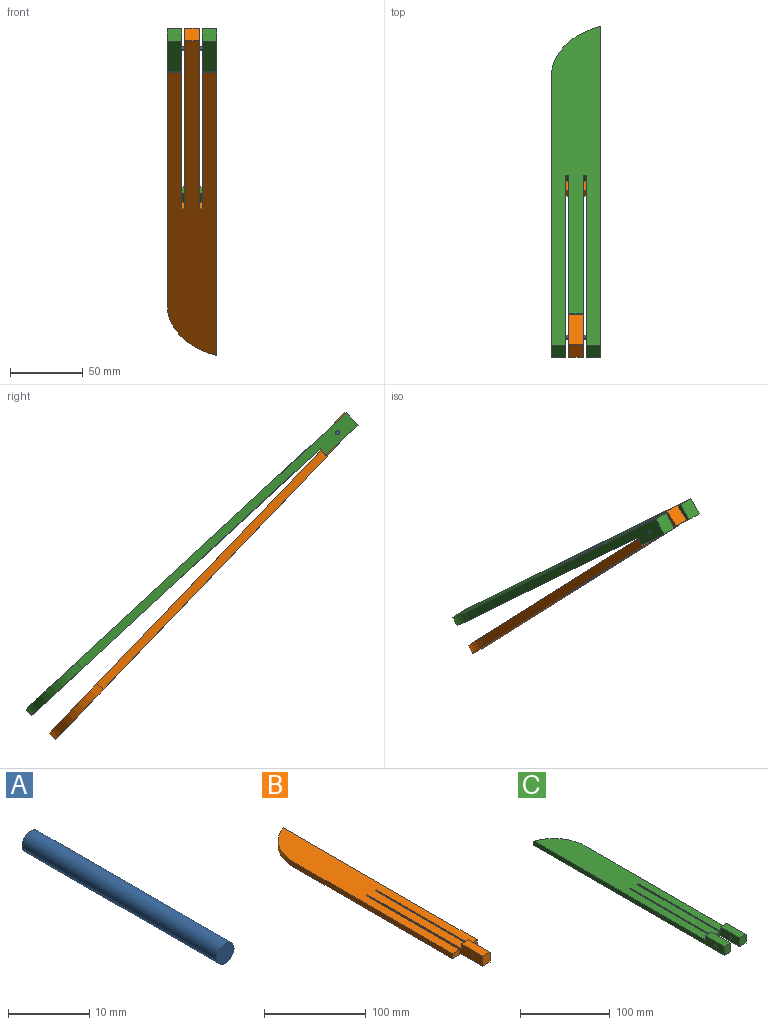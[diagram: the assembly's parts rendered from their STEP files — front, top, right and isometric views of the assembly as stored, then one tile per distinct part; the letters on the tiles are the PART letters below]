
ASSEMBLY  parts=3 mates=3
PART A: 3 faces, bbox 3x34x3 mm
  f0: cylinder r=1.5mm len=34mm, axis (0,1,0), area 320.4mm2, adj f1,f2
  f1: plane 3x3mm, normal (0,-1,0), area 7.1mm2, adj f0
  f2: plane 3x3mm, normal (0,1,0), area 7.1mm2, adj f0
PART B: 17 faces, bbox 34x300x12 mm
  f0: plane 270x34mm, normal (0,0,1), area 8226.8mm2, adj f1,f3,f4,f5,f6,f7,f8,f9
  f1: plane 160x12mm, normal (-1,0,0), area 1132.9mm2, adj f0,f2,f11,f12,f14,f15,f16
  f2: plane 12x10mm, normal (0,-1,0), area 120mm2, adj f1,f3,f12,f15
  f3: plane 160x12mm, normal (1,0,0), area 1132.9mm2, adj f0,f2,f4,f12,f14,f15,f16
  f4: plane 6x2mm, normal (0,-1,0), area 12mm2, adj f0,f3,f5,f12
  f5: plane 130x6mm, normal (-1,0,0), area 780mm2, adj f0,f4,f6,f12
  f6: plane 10x6mm, normal (0,-1,0), area 60mm2, adj f0,f5,f7,f12
  f7: plane 270x6mm, normal (1,0,0), area 1620mm2, adj f0,f6,f12,f13
  f8: plane 222.63x6mm, normal (-1,0,0), area 1335.8mm2, adj f0,f9,f12,f13
  f9: plane 10x6mm, normal (0,-1,0), area 60mm2, adj f0,f8,f10,f12
  f10: plane 130x6mm, normal (1,0,0), area 780mm2, adj f0,f9,f11,f12
  f11: plane 6x2mm, normal (0,-1,0), area 12mm2, adj f0,f1,f10,f12
  f12: plane 300x34mm, normal (0,0,-1), area 8526.8mm2, adj f1,f2,f3,f4,f5,f6,f7,f8
  f13: cylinder r=50mm len=47.37mm, axis (0,0,-1), area 373.5mm2, adj f0,f7,f8,f12
  f14: plane 10x6mm, normal (0,1,0), area 60mm2, adj f0,f1,f3,f15
  f15: plane 30x10mm, normal (0,0,1), area 300mm2, adj f1,f2,f3,f14
  f16: cylinder r=1.5mm len=10mm, axis (-1,0,0), area 94.2mm2, adj f1,f3
PART C: 20 faces, bbox 34x300x12 mm
  f0: plane 270x34mm, normal (0,0,1), area 8226.8mm2, adj f1,f2,f3,f4,f5,f6,f7,f9
  f1: plane 160x12mm, normal (1,0,0), area 1132.9mm2, adj f0,f2,f11,f12,f13,f14,f18
  f2: plane 6x2mm, normal (0,-1,0), area 12mm2, adj f0,f1,f3,f12
  f3: plane 130x6mm, normal (-1,0,0), area 780mm2, adj f0,f2,f4,f12
  f4: plane 10x6mm, normal (0,-1,0), area 60mm2, adj f0,f3,f5,f12
  f5: plane 130x6mm, normal (1,0,0), area 780mm2, adj f0,f4,f6,f12
  f6: plane 6x2mm, normal (0,-1,0), area 12mm2, adj f0,f5,f7,f12
  f7: plane 160x12mm, normal (-1,0,0), area 1132.9mm2, adj f0,f6,f8,f12,f15,f16,f17
  f8: plane 12x10mm, normal (0,-1,0), area 120mm2, adj f7,f9,f12,f16
  f9: plane 252.63x12mm, normal (1,0,0), area 1688.7mm2, adj f0,f8,f12,f15,f16,f17,f19
  f10: plane 300x12mm, normal (-1,0,0), area 1972.9mm2, adj f0,f11,f12,f13,f14,f18,f19
  f11: plane 12x10mm, normal (0,-1,0), area 120mm2, adj f1,f10,f12,f14
  f12: plane 300x34mm, normal (0,0,-1), area 8826.8mm2, adj f1,f2,f3,f4,f5,f6,f7,f8
  f13: plane 10x6mm, normal (0,1,0), area 60mm2, adj f0,f1,f10,f14
  f14: plane 30x10mm, normal (0,0,1), area 300mm2, adj f1,f10,f11,f13
  f15: plane 10x6mm, normal (0,1,0), area 60mm2, adj f0,f7,f9,f16
  f16: plane 30x10mm, normal (0,0,1), area 300mm2, adj f7,f8,f9,f15
  f17: cylinder r=1.5mm len=10mm, axis (-1,0,0), area 94.2mm2, adj f7,f9
  f18: cylinder r=1.5mm len=10mm, axis (-1,0,0), area 94.2mm2, adj f1,f10
  f19: cylinder r=50mm len=47.37mm, axis (0,0,-1), area 373.5mm2, adj f0,f9,f10,f12
PLACE A rot(axis=(0.71,0.71,0),180deg) t=(-91.34,-142.05,158.06)mm fixed
PLACE B rot(axis=(-1,0,0),46.2deg) t=(-89.25,-105.56,111.53)mm
PLACE C rot(axis=(0,0.93,-0.36),180deg) t=(-91.34,-37.93,70.11)mm
MATE revolute C.f17 <-> A.f0  axis (1,0,0) through (-74.34,-142.05,158.28)mm
MATE cylindrical A.f0 <-> C.f17  axis (1,0,0) through (-74.34,-142.05,158.28)mm
MATE revolute B.f16 <-> A.f0  axis (-1,0,0) through (-86.34,-142.05,158.28)mm
